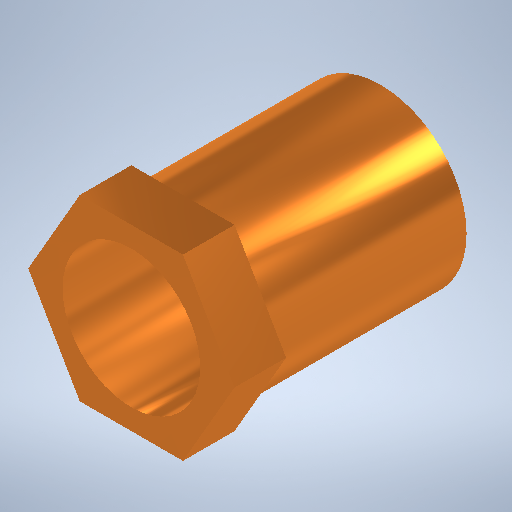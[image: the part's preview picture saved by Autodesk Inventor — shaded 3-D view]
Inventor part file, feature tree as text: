
AUTODESK INVENTOR PART (.ipt)
format: ipt  version: 2025 (Build 290162010, 162A)  size: 264,704 bytes
history: native  units: mm
features: sketch x3, extrude x2, hole x1
ambient origin geometry x8: Origin, YZ Plane, XZ Plane, XY Plane, X Axis, Y Axis, Z Axis, Center Point
bodies: Body1 (feature_tree)
feature tree (6):
  extrude  "Extrusion3"  Depth=3.0mm TaperAngle=0.0deg
  extrude  "Extrusion4"  Depth=11.5mm TaperAngle=0.0deg
  hole  "Hole1"  [1 undecoded]
  sketch  "Skizze1"  dims[d5=12.0mm d10=3.0mm d11=0.0mm]
  sketch  "Sketch4"  dims[d12=10.0mm d13=11.5mm d14=0.0mm]
  sketch  "Sketch5"  dims[d15=8.0mm d16=6.0mm d17=10.0mm d18=5.0mm d19=90.0deg d20=8.0mm d21=0.0mm]
note: 1 required parameter value undecoded (feature->parameter linkage not recoverable at this tier; creation-order binding heuristic only, values carry confidence <= 0.55)
